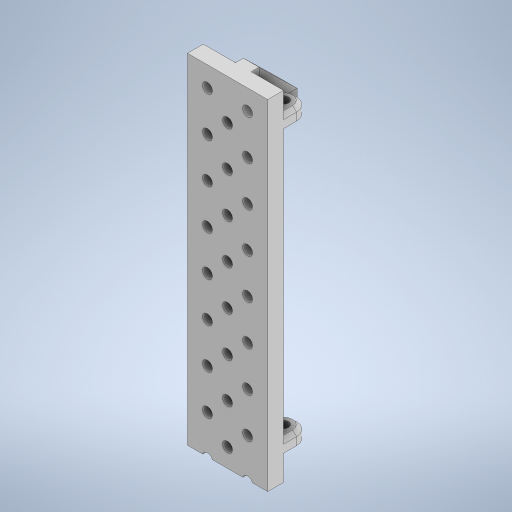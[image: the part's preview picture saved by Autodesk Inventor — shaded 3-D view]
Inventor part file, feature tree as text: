
AUTODESK INVENTOR PART (.ipt)
format: ipt  version: 2024 (Build 280153000, 153)  size: 929,280 bytes
history: native  units: mm
features: extrude x9, projected_geometry x8, sketch x5, other x2, mirror x1, plane x1, chamfer x1, loft x1
ambient origin geometry x8: Origin, YZ Plane, XZ Plane, XY Plane, X Axis, Y Axis, Z Axis, Center Point
bodies: Solid1 (feature_tree)
feature tree (28):
  extrude  "Extrusion1"  Depth=10.0mm
  extrude  "Extrusion2"  Depth=16.002mm
  extrude  "Extrusion3"  Depth=16.002mm
  mirror  "Mirror1"
  extrude  "Extrusion4"  Depth=5.5118mm
  extrude  "Extrusion22"  Depth=2.9972mm
  extrude  "Extrusion23"  Depth=6.096mm
  extrude  "Extrusion24"  Depth=8.001mm
  extrude  "Extrusion14"  Depth=6.5mm
  plane  "Work Plane2"
  extrude  "Extrusion25"  Depth=152.5mm
  chamfer  "Chamfer1"  Distance=60.0mm
  loft  "Loft6"
  sketch  "Sketch1"  dims[d0=5.0mm d1=10.0mm]
  projected_geometry  "Projected Loop1"
  projected_geometry  "Projected Loop2"
  projected_geometry  "Projected Loop3"
  projected_geometry  "Projected Loop17"
  sketch  "Sketch23"  dims[d2=122.8852mm d3=16.002mm]
  projected_geometry  "Projected Loop30"
  sketch  "Sketch24"  dims[d4=2.9972mm d5=16.002mm]
  projected_geometry  "Projected Loop31"
  sketch  "Sketch25"  dims[d6=11.938mm d7=5.5118mm]
  projected_geometry  "Projected Loop32"
  sketch  "Sketch26"  dims[d8=5.0038mm d9=2.9972mm d10=6.096mm d11=8.001mm d12=6.5mm d13=152.5mm d14=60.0mm d15=215.0mm d16=50.8mm d17=8.25mm d18=16.5mm d19=25.4mm d20=6.35mm d21=127.8852mm d22=10.0076mm d23=20.0mm d24=1.0mm d25=1.0mm d26=1.0mm d27=1.0mm d28=1.0mm d29=1.0mm d30=1.0mm d31=1.0mm d32=1.0mm d33=1.0mm d34=1.0mm d35=1.0mm d36=1.0mm d37=1.0mm d38=1.0mm d39=1.0mm d40=1.0mm d41=3.0mm d42=3.0mm d43=3.0mm d44=3.0mm d45=3.0mm d46=3.0mm d47=3.0mm d48=3.0mm d49=3.0mm d50=3.0mm d51=3.0mm d52=3.0mm d53=3.0mm d54=3.0mm d55=3.0mm d56=3.0mm d57=3.0mm d58=3.0mm d59=3.0mm d60=3.0mm d61=3.0mm d62=3.0mm d63=3.0mm d64=3.0mm d65=3.0mm d66=3.0mm d67=3.0mm d68=3.0mm d69=3.0mm d70=3.0mm d71=3.0mm d72=3.0mm d73=3.0mm d74=3.0mm d75=3.0mm d76=3.0mm d77=3.0mm d78=3.0mm d79=3.0mm d80=3.0mm d81=3.0mm d82=25.4mm d83=50.8mm d84=215.0mm d86=25.4mm d88=12.7mm d89=12.7mm d90=6.35mm d91=6.35mm d92=12.7mm d93=12.7mm d94=45.0deg d95=45.0deg d96=6.35mm d97=120.0mm d99=25.4mm d100=10.0mm d102=10.0mm d104=10.0mm d105=0.0mm d106=10.0mm d107=13.5128mm d108=10.0mm d109=13.5128mm d110=16.5mm d111=0.0mm d112=16.5mm d113=8.25mm d114=8.25mm d115=16.5mm d116=16.5mm d117=8.25mm d118=6.5mm d119=25.4mm d120=215.0mm d121=0.0mm d122=10.0076mm d123=16.096mm d124=8.048mm d125=182.5mm d126=26.002mm d127=0.0mm d186=50.8mm d187=10.0mm d188=30.4mm d189=0.0mm d190=10.0mm d191=5.0mm d192=0.0mm d196=2.5mm d197=2.0mm d198=45.0deg d236=0.0mm d237=16.096mm d238=26.002mm d239=6.096mm d240=8.001mm d241=6.096mm d242=8.001mm d243=17.0015mm d244=11.096mm d245=0.0mm d246=0.0mm d247=1.0mm d248=0.0mm d249=1.0mm d250=0.0mm d251=3.048mm d252=2.9972mm d253=8.001mm d254=4.0005mm d255=11.008mm d256=5.504mm d257=25.76mm d258=0.0mm d259=0.0mm d260=90.0deg d261=0.0mm d262=90.0deg d199=0.872665mm d216=0.5mm d217=0.872665mm d218=0.5mm d219=0.872665mm d228=0.5mm d229=0.872665mm d230=0.5mm d231=0.872665mm]
  projected_geometry  "Projected Loop33"
  other  "Edges11"
  other  "Edges12"
